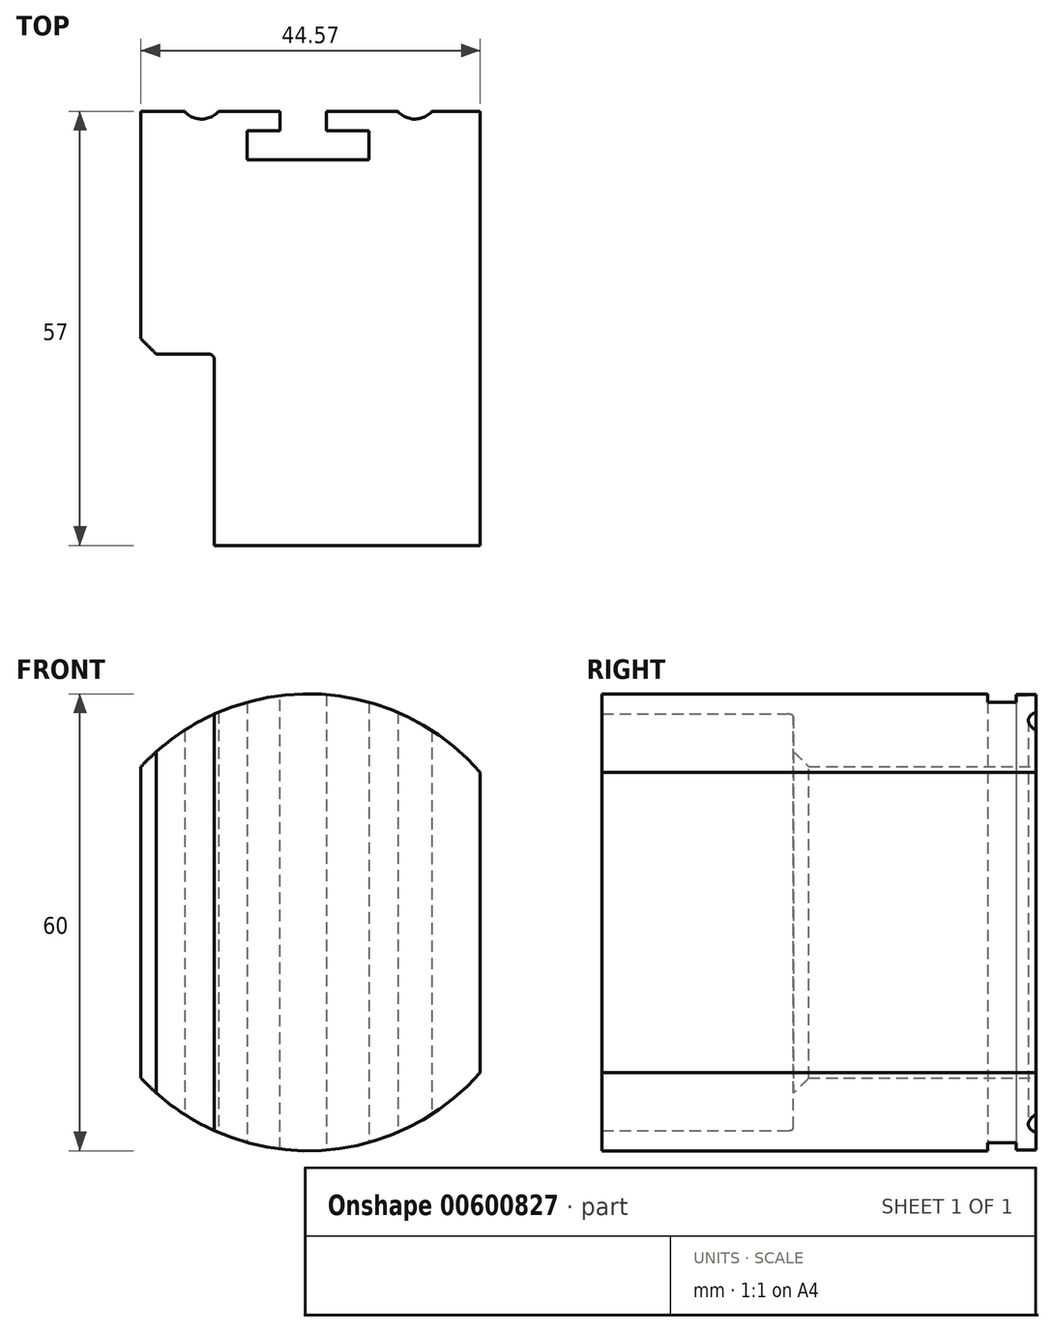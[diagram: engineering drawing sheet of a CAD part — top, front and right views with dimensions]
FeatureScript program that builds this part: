
annotation { "Feature Type Name" : "Feature", "Feature Type Description" : "" }
export const myFeature = defineFeature(function(context is Context, id is Id, definition is map)
    precondition{}
    {
        {
            var Q0;
            Q0=qCreatedBy(makeId("Front.planeOp"),FACE);
            var sketch = newSketch(context, id + "F0", { "sketchPlane" : qUnion([Q0])});
            skCircle(sketch, "E0", {"center": v(0, 0) * mm, "radius": 30 * mm});
            skSolve(sketch);
        }
        {
            var Q0;
            Q0 = qSketchRegion(id + "F0", true);
            extrude(context, id + "F1", {"entities" : qUnion([Q0]), "depth" : 65 * mm, "offsetDistance" : 25 * mm});
        }
        {
            var Q0;
            Q0=makeQuery(id+"F1.opExtrude","CAP_FACE",FACE,{"disambiguationData":[OSD([sQuery(id+"F0.wireOp",EDGE,"E0")])],"isStart":false});
            var sketch = newSketch(context, id + "F2", { "sketchPlane" : qUnion([Q0])});
            skLineSegment(sketch, "E1.right", {"start": v(-21.96, 0) * mm, "end": v(-21.96, 35.53) * mm});
            skLineSegment(sketch, "E2.left", {"start": v(1.54, 0) * mm, "end": v(1.54, 0) * mm});
            skLineSegment(sketch, "E2.right", {"start": v(4.7, 0) * mm, "end": v(4.7, 0) * mm});
            skLineSegment(sketch, "E3.right", {"start": v(22.61, 35.53) * mm, "end": v(22.61, -36.65) * mm});
            skLineSegment(sketch, "E4.bottom", {"start": v(1.54, 9.88) * mm, "end": v(0, 9.88) * mm});
            skLineSegment(sketch, "E4.top", {"start": v(1.54, 0) * mm, "end": v(0, 0) * mm});
            skLineSegment(sketch, "E5.bottom", {"start": v(22.61, 35.53) * mm, "end": v(48.32, 35.53) * mm});
            skLineSegment(sketch, "E5.top", {"start": v(22.61, -36.84) * mm, "end": v(48.32, -36.84) * mm});
            skLineSegment(sketch, "E5.right", {"start": v(48.32, 35.53) * mm, "end": v(48.32, -36.84) * mm});
            skLineSegment(sketch, "E6.bottom", {"start": v(-21.96, 35.53) * mm, "end": v(-38.48, 35.53) * mm});
            skLineSegment(sketch, "E6.top", {"start": v(-21.96, -36.84) * mm, "end": v(-38.48, -36.84) * mm});
            skLineSegment(sketch, "E6.left", {"start": v(-21.96, 35.53) * mm, "end": v(-21.96, -36.84) * mm});
            skLineSegment(sketch, "E6.right", {"start": v(-38.48, 35.53) * mm, "end": v(-38.48, -36.84) * mm});
            skLineSegment(sketch, "E7", {"start": v(22.61, -36.65) * mm, "end": v(22.61, -36.84) * mm});
            skSolve(sketch);
        }
        {
            var Q0;
            Q0 = qSketchRegion(id + "F2", true);
            extrude(context, id + "F3", {"entities" : qUnion([Q0]), "operationType" : NewBodyOperationType.REMOVE, "oppositeDirection" : true, "depth" : 100 * mm, "offsetDistance" : 25 * mm});
        }
        {
            var Q0;
            Q0=qCreatedBy(makeId("Top.planeOp"),FACE);
            var sketch = newSketch(context, id + "F4", { "sketchPlane" : qUnion([Q0])});
            skLineSegment(sketch, "E8", {"start": v(-3.7, 0) * mm, "end": v(-3.7, -2.57) * mm});
            skLineSegment(sketch, "E9", {"start": v(-3.7, -2.57) * mm, "end": v(-8, -2.57) * mm});
            skLineSegment(sketch, "E10", {"start": v(-8, -2.57) * mm, "end": v(-8, -6.34) * mm});
            skLineSegment(sketch, "E11", {"start": v(-8, -6.34) * mm, "end": v(8, -6.34) * mm});
            skLineSegment(sketch, "E12", {"start": v(8, -6.34) * mm, "end": v(8, -2.57) * mm});
            skLineSegment(sketch, "E13", {"start": v(8, -2.57) * mm, "end": v(2.38, -2.57) * mm});
            skLineSegment(sketch, "E14", {"start": v(2.38, -2.57) * mm, "end": v(2.38, 0) * mm});
            skLineSegment(sketch, "E15", {"start": v(2.38, 0) * mm, "end": v(2.38, 1.41) * mm});
            skLineSegment(sketch, "E16", {"start": v(2.38, 1.41) * mm, "end": v(-3.7, 1.41) * mm});
            skLineSegment(sketch, "E17", {"start": v(-3.7, 1.41) * mm, "end": v(-3.7, 0) * mm});
            skSolve(sketch);
        }
        {
            var Q0;
            Q0 = qSketchRegion(id + "F4", true);
            extrude(context, id + "F5", {"entities" : qUnion([Q0]), "operationType" : NewBodyOperationType.REMOVE, "endBound" : BoundingType.THROUGH_ALL, "depth" : 25 * mm, "offsetDistance" : 25 * mm});
        }
        {
            var Q0;
            Q0 = qSketchRegion(id + "F4", true);
            extrude(context, id + "F6", {"entities" : qUnion([Q0]), "operationType" : NewBodyOperationType.REMOVE, "endBound" : BoundingType.THROUGH_ALL, "oppositeDirection" : true, "depth" : 25 * mm, "offsetDistance" : 25 * mm});
        }
        {
            var Q0;
            Q0=qCreatedBy(makeId("Top.planeOp"),FACE);
            var sketch = newSketch(context, id + "F7", { "sketchPlane" : qUnion([Q0])});
            skLineSegment(sketch, "E18.bottom", {"start": v(-12.31, -68.4) * mm, "end": v(-27.75, -68.4) * mm});
            skLineSegment(sketch, "E18.top", {"start": v(-12.31, -31.85) * mm, "end": v(-27.75, -31.85) * mm});
            skLineSegment(sketch, "E18.left", {"start": v(-12.31, -68.4) * mm, "end": v(-12.31, -31.85) * mm});
            skLineSegment(sketch, "E18.right", {"start": v(-27.75, -68.4) * mm, "end": v(-27.75, -31.85) * mm});
            skSolve(sketch);
        }
        {
            var Q0;
            Q0 = qSketchRegion(id + "F7", true);
            extrude(context, id + "F8", {"entities" : qUnion([Q0]), "operationType" : NewBodyOperationType.REMOVE, "endBound" : BoundingType.THROUGH_ALL, "oppositeDirection" : true, "depth" : 25 * mm, "offsetDistance" : 25 * mm});
        }
        {
            var Q0;
            Q0 = qSketchRegion(id + "F7", true);
            extrude(context, id + "F9", {"entities" : qUnion([Q0]), "operationType" : NewBodyOperationType.REMOVE, "endBound" : BoundingType.THROUGH_ALL, "depth" : 25 * mm, "offsetDistance" : 25 * mm});
        }
        {
            var Q0;
            Q0=makeQuery(id+"F9.boolean.opBoolean","INTERSECT",EDGE,{"derivedFrom":[makeQuery(id+"F3.boolean.opBoolean","COPY",FACE,{"derivedFrom":makeQuery(id+"F3.opExtrude","SWEPT_FACE",FACE,{"disambiguationData":[OSD([sQuery(id+"F2.wireOp",EDGE,"E6.left")])]})}),makeQuery(id+"F9.opExtrude","SWEPT_FACE",FACE,{"disambiguationData":[OSD([sQuery(id+"F7.wireOp",EDGE,"E18.top")])]})]});
            chamfer(context, id + "F10", {"entities" : qUnion([Q0]), "width" : 2 * mm, "tangentPropagation" : true});
        }
        {
            var Q0;
            {var subQ0=sQuery(id+"F7.wireOp",EDGE,"E18.left");var subQ1=sQuery(id+"F7.wireOp",EDGE,"E18.top");Q0=makeQuery(id+"F9.boolean.opBoolean","MERGE",EDGE,{"derivedFrom":[makeQuery(id+"F8.boolean.opBoolean","COPY",EDGE,{"derivedFrom":makeQuery(id+"F8.opExtrude","SWEPT_EDGE",EDGE,{"disambiguationData":[OSD([subQ1,subQ0])]})}),makeQuery(id+"F9.opExtrude","SWEPT_EDGE",EDGE,{"disambiguationData":[OSD([subQ1,subQ0])]})]});}
            fillet(context, id + "F11", {"entities" : qUnion([Q0]), "radius" : 0.8 * mm, "tangentPropagation" : true, "allowEdgeOverflow" : false});
        }
        {
            var Q0;
            Q0=qCreatedBy(makeId("Top.planeOp"),FACE);
            var sketch = newSketch(context, id + "F12", { "sketchPlane" : qUnion([Q0])});
            skCircle(sketch, "E19", {"center": v(-14, 2) * mm, "radius": 3 * mm});
            skCircle(sketch, "E20", {"center": v(14, 2) * mm, "radius": 3 * mm});
            skSolve(sketch);
        }
        {
            var Q0;
            Q0 = qSketchRegion(id + "F12", true);
            extrude(context, id + "F13", {"entities" : qUnion([Q0]), "operationType" : NewBodyOperationType.REMOVE, "endBound" : BoundingType.THROUGH_ALL, "depth" : 40 * mm, "offsetDistance" : 25 * mm, "hasSecondDirection" : true, "secondDirectionOppositeDirection" : true, "secondDirectionDepth" : 40 * mm});
        }
        {
            var Q0;
            Q0=makeQuery(id+"F1.opExtrude","CAP_FACE",FACE,{"disambiguationData":[OSD([sQuery(id+"F0.wireOp",EDGE,"E0")])],"isStart":false});
            extrude(context, id + "F14", {"entities" : qUnion([Q0]), "operationType" : NewBodyOperationType.ADD, "oppositeDirection" : true, "depth" : 8 * mm, "offsetDistance" : 25 * mm});
        }
        {
            var Q0;
            Q0=makeQuery(id+"F1.opExtrude","CAP_FACE",FACE,{"disambiguationData":[OSD([sQuery(id+"F0.wireOp",EDGE,"E0")])],"isStart":false});
            extrude(context, id + "F15", {"entities" : qUnion([Q0]), "operationType" : NewBodyOperationType.ADD, "oppositeDirection" : true, "depth" : 8 * mm, "offsetDistance" : 25 * mm});
        }
        {
            var Q0;
            Q0=makeQuery(id+"F1.opExtrude","CAP_FACE",FACE,{"disambiguationData":[OSD([sQuery(id+"F0.wireOp",EDGE,"E0")])],"isStart":false});
            extrude(context, id + "F16", {"entities" : qUnion([Q0]), "operationType" : NewBodyOperationType.REMOVE, "oppositeDirection" : true, "depth" : 8 * mm, "offsetDistance" : 25 * mm});
        }
    });
